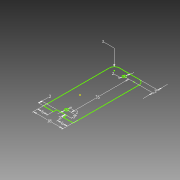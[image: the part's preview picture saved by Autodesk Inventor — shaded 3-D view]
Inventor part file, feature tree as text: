
AUTODESK INVENTOR PART (.ipt)
format: ipt  version: 2012 (Build 160160000, 160)  size: 69,120 bytes
history: native  units: mm
features: sketch x1
ambient origin geometry x8: Origin, YZ Plane, XZ Plane, XY Plane, X Axis, Y Axis, Z Axis, Center Point
feature tree (1):
  sketch  "Sketch1"  dims[d0=18.0mm d1=2.0mm d2=2.0mm d3=35.0mm d4=3.0mm d6=3.0mm d11=6.0mm d12=6.0mm d13=2.0mm d14=2.0mm d15=3.0mm]
